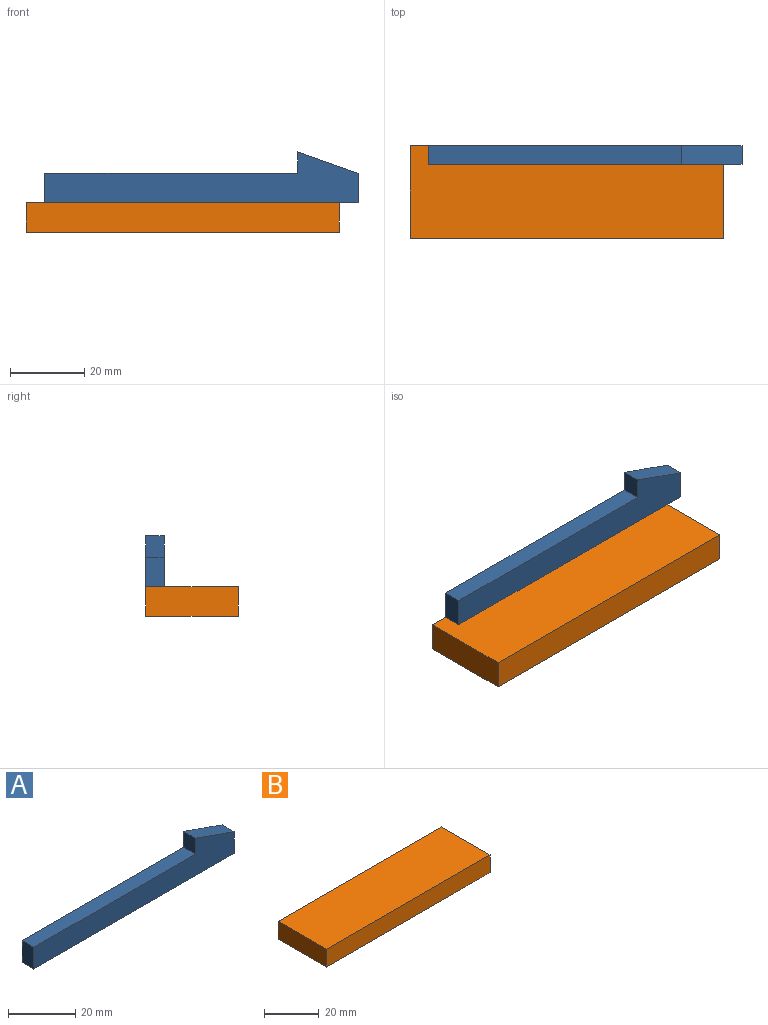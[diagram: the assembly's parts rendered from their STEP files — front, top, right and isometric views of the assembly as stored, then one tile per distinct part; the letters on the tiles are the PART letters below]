
ASSEMBLY  parts=2 mates=1
PART A: 8 faces, bbox 84.3x5x13.7 mm
  f0: plane 7.93x5mm, normal (1,0,0), area 39.7mm2, adj f1,f5,f6,f7
  f1: plane 16.28x5.77mm, normal (0.33,0,0.94), area 86.4mm2, adj f0,f2,f6,f7
  f2: plane 5.77x5mm, normal (-1,0,0), area 28.8mm2, adj f1,f3,f6,f7
  f3: plane 68.03x5mm, normal (0,0,1), area 340.2mm2, adj f2,f4,f6,f7
  f4: plane 7.93x5mm, normal (-1,0,0), area 39.7mm2, adj f3,f5,f6,f7
  f5: plane 84.31x5mm, normal (0,0,-1), area 421.6mm2, adj f0,f4,f6,f7
  f6: plane 84.31x13.7mm, normal (0,-1,0), area 715.7mm2, adj f0,f1,f2,f3,f4,f5
  f7: plane 84.31x13.7mm, normal (0,1,0), area 715.7mm2, adj f0,f1,f2,f3,f4,f5
PART B: 6 faces, bbox 84.3x25x7.9 mm
  f0: plane 84.31x25mm, normal (0,0,1), area 2107.8mm2, adj f1,f3,f4,f5
  f1: plane 25x7.93mm, normal (-1,0,0), area 198.3mm2, adj f0,f2,f4,f5
  f2: plane 84.31x25mm, normal (0,0,-1), area 2107.8mm2, adj f1,f3,f4,f5
  f3: plane 25x7.93mm, normal (1,0,0), area 198.3mm2, adj f0,f2,f4,f5
  f4: plane 84.31x7.93mm, normal (0,1,0), area 668.8mm2, adj f0,f1,f2,f3
  f5: plane 84.31x7.93mm, normal (0,-1,0), area 668.8mm2, adj f0,f1,f2,f3
PLACE A t=(43.96,0,-12.08)mm
PLACE B rot(axis=(1,0,0),180deg) t=(38.89,0,27.94)mm
MATE pin_slot B.f2 <-> A.f5  axis (0,0,1) through (42.16,0,7.93)mm
